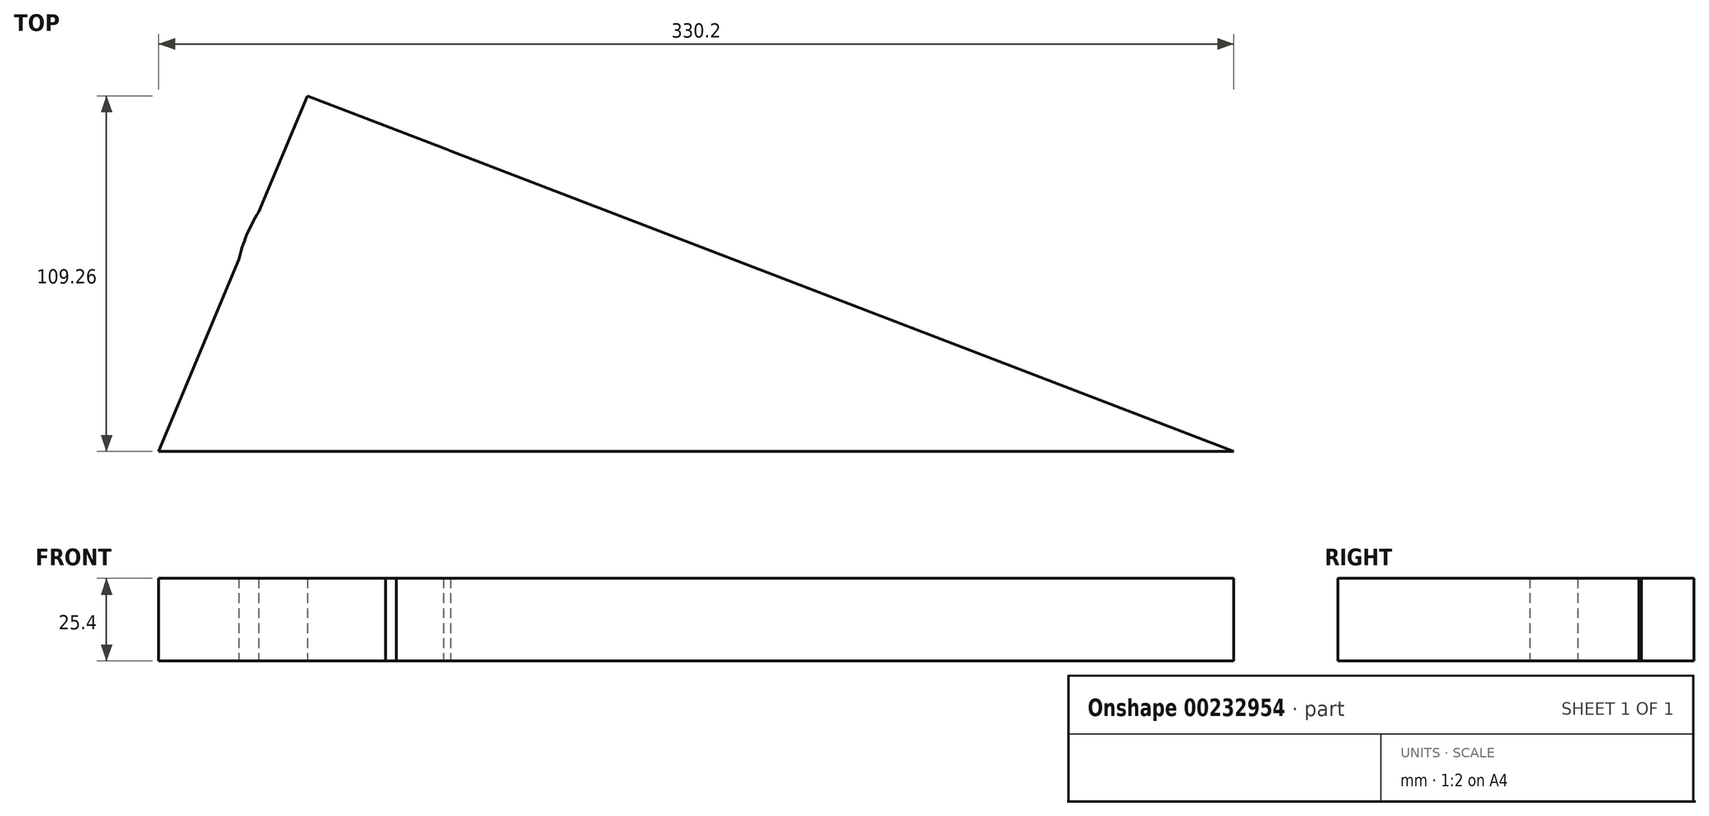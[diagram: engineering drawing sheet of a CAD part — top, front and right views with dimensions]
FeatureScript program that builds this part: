
annotation { "Feature Type Name" : "Feature", "Feature Type Description" : "" }
export const myFeature = defineFeature(function(context is Context, id is Id, definition is map)
    precondition{}
    {
        {
            var Q0;
            Q0=qCreatedBy(makeId("Top.planeOp"),FACE);
            var sketch = newSketch(context, id + "F0", { "sketchPlane" : qUnion([Q0])});
            skLineSegment(sketch, "E0", {"start": v(-169.06, -79.73) * mm, "end": v(161.14, -79.73) * mm});
            skLineSegment(sketch, "E1", {"start": v(161.14, -79.73) * mm, "end": v(-123.42, 29.5) * mm});
            skLineSegment(sketch, "E2", {"start": v(-169.06, -79.73) * mm, "end": v(-123.42, 29.5) * mm});
            skCircle(sketch, "E3", {"center": v(-97.72, -31.76) * mm, "radius": 48 * mm});
            skPoint(sketch, "E3.first.point", {"position": v(-81.66, 13.47) * mm});
            skPoint(sketch, "E3.second.point", {"position": v(-96.04, -79.73) * mm});
            skPoint(sketch, "E3.third.point", {"position": v(-144.46, -20.86) * mm});
            skSolve(sketch);
        }
        {
            var Q0;
            Q0 = qSketchRegion(id + "F0", true);
            extrude(context, id + "F1", {"entities" : qUnion([Q0]), "depth" : 25.4 * mm});
        }
    });
